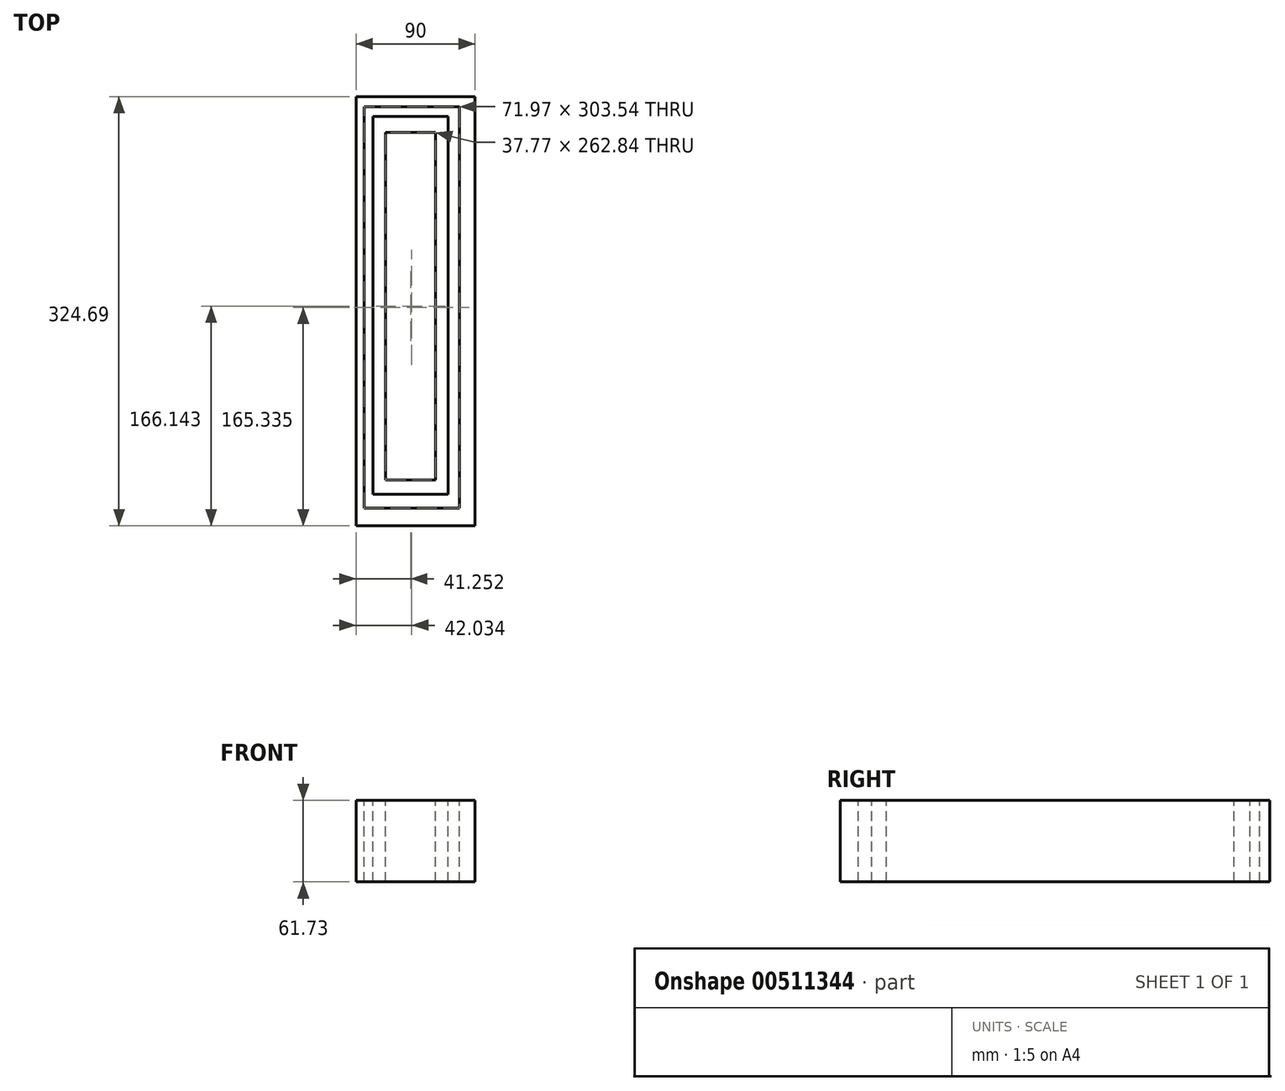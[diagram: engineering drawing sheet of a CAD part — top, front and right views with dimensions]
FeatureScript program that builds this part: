
annotation { "Feature Type Name" : "Feature", "Feature Type Description" : "" }
export const myFeature = defineFeature(function(context is Context, id is Id, definition is map)
    precondition{}
    {
        {
            var Q0;
            Q0=qCreatedBy(makeId("Right.planeOp"),FACE);
            var sketch = newSketch(context, id + "F0", { "sketchPlane" : qUnion([Q0])});
            skLineSegment(sketch, "E0.bottom", {"start": v(-35.77, 33.77) * mm, "end": v(-360.46, 33.77) * mm});
            skLineSegment(sketch, "E0.top", {"start": v(-35.77, 95.5) * mm, "end": v(-360.46, 95.5) * mm});
            skLineSegment(sketch, "E0.left", {"start": v(-35.77, 33.77) * mm, "end": v(-35.77, 95.5) * mm});
            skLineSegment(sketch, "E0.right", {"start": v(-360.46, 33.77) * mm, "end": v(-360.46, 95.5) * mm});
            skPoint(sketch, "E0.middle", {"position": v(-198.11, 64.64) * mm});
            skSolve(sketch);
        }
        {
            var Q0;
            Q0=makeQuery(id+"F0.imprint","IMPRINT",FACE,{"disambiguationData":[TD([[makeQuery(id+"F0.imprint","IMPRINT",EDGE,{"derivedFrom":sQuery(id+"F0.wireOp",EDGE,"E0.bottom")}),-1.0]])]});
            extrude(context, id + "F1", {"entities" : qUnion([Q0]), "depth" : 90 * mm});
        }
        {
            var Q0;
            Q0=makeQuery(id+"F1.opExtrude","SWEPT_FACE",FACE,{"disambiguationData":[OSD([sQuery(id+"F0.wireOp",EDGE,"E0.top")])]});
            var sketch = newSketch(context, id + "F2", { "sketchPlane" : qUnion([Q0])});
            skLineSegment(sketch, "E1.bottom", {"start": v(6.05, -43.35) * mm, "end": v(78.02, -43.35) * mm});
            skLineSegment(sketch, "E1.top", {"start": v(6.05, -346.9) * mm, "end": v(78.02, -346.9) * mm});
            skLineSegment(sketch, "E1.left", {"start": v(6.05, -43.35) * mm, "end": v(6.05, -346.9) * mm});
            skLineSegment(sketch, "E1.right", {"start": v(78.02, -43.35) * mm, "end": v(78.02, -346.9) * mm});
            skSolve(sketch);
        }
        {
            var Q0;
            Q0=makeQuery(id+"F2.imprint","IMPRINT",FACE,{"disambiguationData":[TD([[makeQuery(id+"F2.imprint","IMPRINT",EDGE,{"derivedFrom":sQuery(id+"F2.wireOp",EDGE,"E1.bottom")}),-1.0]])]});
            var sketch = newSketch(context, id + "F3", { "sketchPlane" : qUnion([Q0])});
            skLineSegment(sketch, "E2.bottom", {"start": v(12.85, -50.77) * mm, "end": v(69.59, -50.77) * mm});
            skLineSegment(sketch, "E2.top", {"start": v(12.85, -336.65) * mm, "end": v(69.59, -336.65) * mm});
            skLineSegment(sketch, "E2.left", {"start": v(12.85, -50.77) * mm, "end": v(12.85, -336.65) * mm});
            skLineSegment(sketch, "E2.right", {"start": v(69.59, -50.77) * mm, "end": v(69.59, -336.65) * mm});
            skLineSegment(sketch, "E3.bottom", {"start": v(22.37, -62.9) * mm, "end": v(60.14, -62.9) * mm});
            skLineSegment(sketch, "E3.top", {"start": v(22.37, -325.73) * mm, "end": v(60.14, -325.73) * mm});
            skLineSegment(sketch, "E3.left", {"start": v(22.37, -62.9) * mm, "end": v(22.37, -325.73) * mm});
            skLineSegment(sketch, "E3.right", {"start": v(60.14, -62.9) * mm, "end": v(60.14, -325.73) * mm});
            skSolve(sketch);
        }
        {
            var Q0;
            Q0=makeQuery(id+"F3.imprint","IMPRINT",FACE,{"disambiguationData":[TD([[makeQuery(id+"F3.imprint","IMPRINT",EDGE,{"derivedFrom":sQuery(id+"F3.wireOp",EDGE,"E2.bottom")}),1.0]])]});
            var Q1;
            Q1=makeQuery(id+"F3.imprint","IMPRINT",FACE,{"disambiguationData":[TD([[makeQuery(id+"F3.imprint","IMPRINT",EDGE,{"derivedFrom":sQuery(id+"F3.wireOp",EDGE,"E3.bottom")}),-1.0]])]});
            extrude(context, id + "F4", {"entities" : qUnion([Q0, Q1]), "operationType" : NewBodyOperationType.REMOVE, "endBound" : BoundingType.THROUGH_ALL, "oppositeDirection" : true, "depth" : 60 * mm});
        }
        {
            var Q0;
            Q0=makeQuery(id+"F2.imprint","IMPRINT",FACE,{"disambiguationData":[TD([[makeQuery(id+"F2.imprint","IMPRINT",EDGE,{"derivedFrom":sQuery(id+"F2.wireOp",EDGE,"E1.bottom")}),-1.0]])]});
            var sketch = newSketch(context, id + "F5", { "sketchPlane" : qUnion([Q0])});
            skCircle(sketch, "E4", {"center": v(39.65, -84.4) * mm, "radius": 18.48 * mm});
            skSolve(sketch);
        }
        {
            var Q0;
            Q0=sQuery(id+"F5.wireOp",EDGE,"E4");
            extrude(context, id + "F6", {"bodyType" : ToolBodyType.SURFACE, "surfaceEntities" : qUnion([Q0]), "oppositeDirection" : true, "depth" : 65 * mm});
        }
    });
